# Revit family: PS-P83T z
name_source: partatom
category: Generic Models
revit_build: Autodesk Revit 2016 (Build: 20150220_1215(x64)
units: mm (PartAtom-declared; Revit-internal decimal feet)

## family parameters
Always vertical = Yes
Can host rebar = No
Cut with Voids When Loaded = No
Part Type = Normal
Room Calculation Point = No
Round Connector Dimension = Use Diameter
Shared = No
Work Plane-Based = No

## types (1)
- Default
    100V Taps = 15, 30, 60
    70V Taps = 7.5, 15, 30, 60
    Coverage Horizontal = 120
    Coverage Vertical = 120
    Depth = 19.7
    Description = 8" 2-way White Pendant Speaker with 70V/100V transformer for commercial applications
    Directivity (DI) = 8.1
    Directivity Factor (Q) = 7.6
    Frequency Range (-10dB) = 41Hz-25kHz
    Frequency Range (-3dB) = 55Hz-20kHz
    Grille = Supplied with bezel-less white grille.
    Height = 11.06
    High-Frequency Driver = 1” (25mm) Cloth Dome, Pivoting, Ferrofluid cooled
    Impedance = 8
    Input Connector = Four pin Euroblock with loop output connections
    Low-Frequency Driver = 8” (203mm) Polypropylene Cone, Butyl Rubber Surround
    Manufacturer = Sonance
    Manufacturer URL = http://www.sonance.com
    Model = PS-P83T
    Part Number = 45136
    Power Handling = 160
    Power Peak = 160
    Product Documentation Link = https://www.sonance.com
    Product Page URL = https://www.sonance.com
    Regulatory Compliance = UL 1480, UL 2239
    SPL Max = 110
    Sensitivity = 90
    Speaker Data Link = https://www.sonance.com
    Supplied Hanging Hardware = 16.4’ (5m) Stainless Steel Cable with Snaphook x 4, Gripple Hanger x 2, Gripple Adjustment Tool x 2
    Suspension Points = Five points, top mounted
    Weight Dimensional = 23.485
    Weight Product = 16.26
    Width = 11.06

## geometry (parser evidence)
native form markers: Sweep x3
no freeform markers — native parametric forms only
